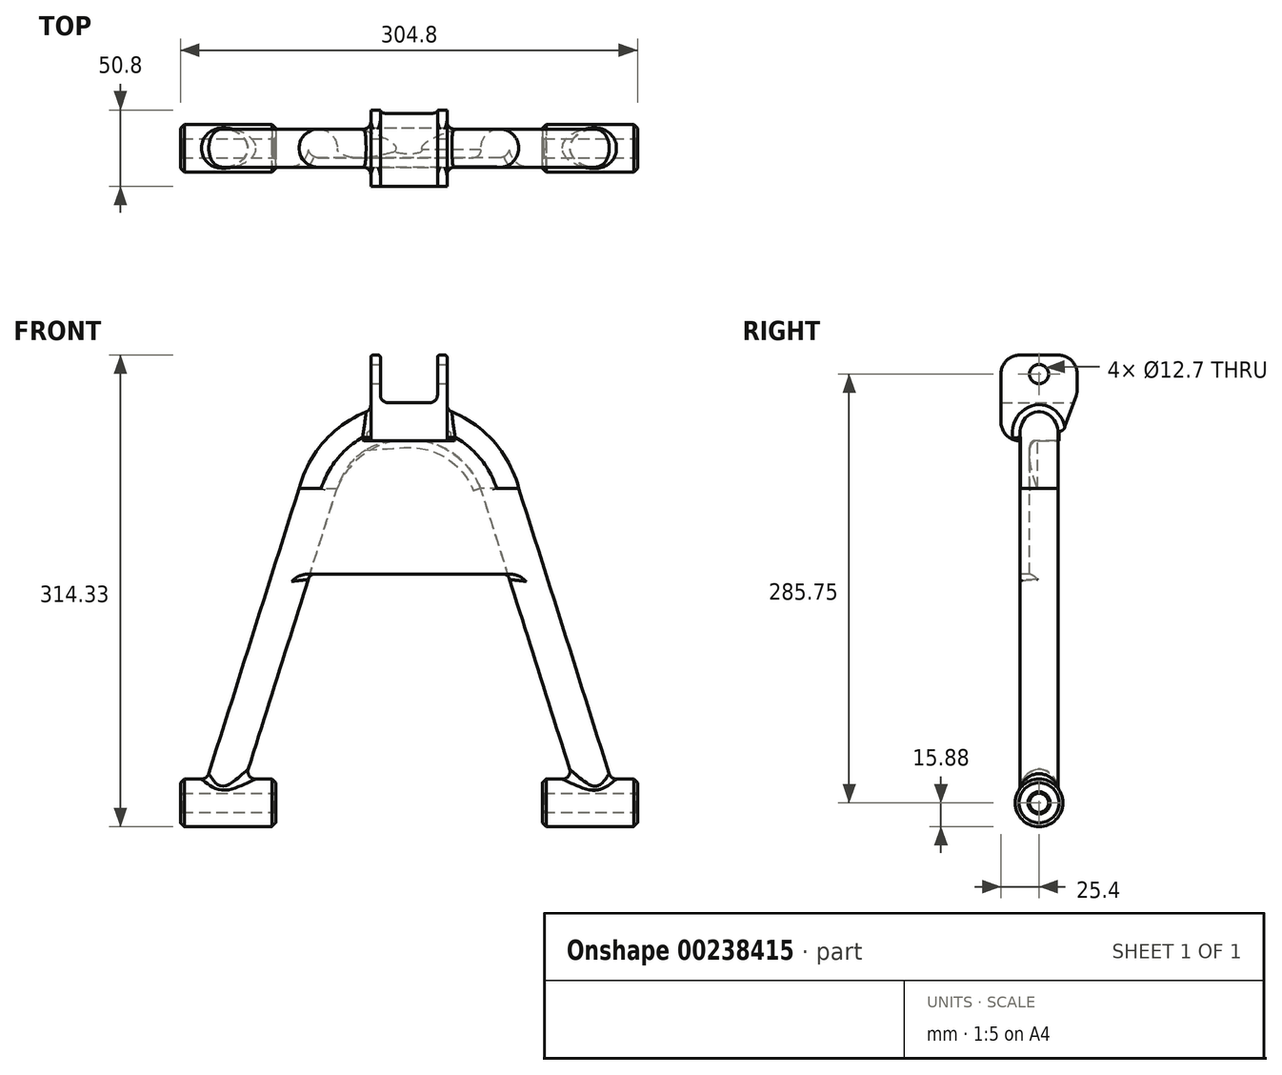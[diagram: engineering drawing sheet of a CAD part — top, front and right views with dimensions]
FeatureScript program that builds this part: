
annotation { "Feature Type Name" : "Feature", "Feature Type Description" : "" }
export const myFeature = defineFeature(function(context is Context, id is Id, definition is map)
    precondition{}
    {
        {
            var Q0;
            Q0=qCreatedBy(makeId("Top.planeOp"),FACE);
            var sketch = newSketch(context, id + "F0", { "sketchPlane" : qUnion([Q0])});
            skLineSegment(sketch, "E0", {"start": v(-127, 0) * mm, "end": v(0, 0) * mm, "construction": true});
            skLineSegment(sketch, "E1", {"start": v(0, 0) * mm, "end": v(127, 0) * mm, "construction": true});
            skCircle(sketch, "E2", {"center": v(-127, 0) * mm, "radius": 12.7 * mm, "construction": true});
            skCircle(sketch, "E3", {"center": v(127, 0) * mm, "radius": 12.7 * mm, "construction": true});
            skSolve(sketch);
        }
        {
            var Q0;
            Q0=qCreatedBy(makeId("Front.planeOp"),FACE);
            var sketch = newSketch(context, id + "F1", { "sketchPlane" : qUnion([Q0])});
            skLineSegment(sketch, "E4", {"start": v(0, 0) * mm, "end": v(0, 254) * mm, "construction": true});
            skArc(sketch, "E5", {"start": v(60.53, 209.69) * mm, "mid": v(0, 254) * mm, "end": v(-60.53, 209.69) * mm, "construction": true});
            skLineSegment(sketch, "E6", {"start": v(0, 0) * mm, "end": v(-127, 0) * mm, "construction": true});
            skLineSegment(sketch, "E7", {"start": v(0, 0) * mm, "end": v(127, 0) * mm, "construction": true});
            skLineSegment(sketch, "E8", {"start": v(-127, 0) * mm, "end": v(-60.53, 209.69) * mm, "construction": true});
            skLineSegment(sketch, "E9", {"start": v(127, 0) * mm, "end": v(60.53, 209.69) * mm, "construction": true});
            skLineSegment(sketch, "E10", {"start": v(-19.05, 271.78) * mm, "end": v(-19.05, 296.93) * mm, "construction": true});
            skLineSegment(sketch, "E11", {"start": v(-20.57, 298.45) * mm, "end": v(-23.88, 298.45) * mm, "construction": true});
            skLineSegment(sketch, "E12", {"start": v(-25.4, 296.93) * mm, "end": v(-25.4, 241.3) * mm, "construction": true});
            skLineSegment(sketch, "E13", {"start": v(-25.4, 241.3) * mm, "end": v(25.4, 241.3) * mm, "construction": true});
            skLineSegment(sketch, "E14", {"start": v(25.4, 241.3) * mm, "end": v(25.4, 296.93) * mm, "construction": true});
            skLineSegment(sketch, "E15", {"start": v(23.88, 298.45) * mm, "end": v(20.57, 298.45) * mm, "construction": true});
            skLineSegment(sketch, "E16", {"start": v(19.05, 296.93) * mm, "end": v(19.05, 271.78) * mm, "construction": true});
            skLineSegment(sketch, "E17", {"start": v(13.97, 266.7) * mm, "end": v(-13.97, 266.7) * mm, "construction": true});
            skPoint(sketch, "E18.orphan", {"position": v(19.05, 254) * mm});
            skPoint(sketch, "E19.visualSharp", {"position": v(-25.4, 298.45) * mm});
            skPoint(sketch, "E20.visualSharp", {"position": v(-19.05, 298.45) * mm});
            skArc(sketch, "E20.filletArc", {"start": v(-19.05, 296.93) * mm, "mid": v(-19.5, 298) * mm, "end": v(-20.57, 298.45) * mm, "construction": true});
            skArc(sketch, "E21.filletArc", {"start": v(-23.88, 298.45) * mm, "mid": v(-24.95, 298) * mm, "end": v(-25.4, 296.93) * mm, "construction": true});
            skPoint(sketch, "E22.visualSharp", {"position": v(19.05, 298.45) * mm});
            skArc(sketch, "E22.filletArc", {"start": v(20.57, 298.45) * mm, "mid": v(19.5, 298) * mm, "end": v(19.05, 296.93) * mm, "construction": true});
            skPoint(sketch, "E23.visualSharp", {"position": v(25.4, 298.45) * mm});
            skArc(sketch, "E23.filletArc", {"start": v(25.4, 296.93) * mm, "mid": v(24.95, 298) * mm, "end": v(23.88, 298.45) * mm, "construction": true});
            skPoint(sketch, "E24.visualSharp", {"position": v(19.05, 266.7) * mm});
            skArc(sketch, "E24.filletArc", {"start": v(13.97, 266.7) * mm, "mid": v(17.56, 268.19) * mm, "end": v(19.05, 271.78) * mm, "construction": true});
            skPoint(sketch, "E25.visualSharp", {"position": v(-19.05, 266.7) * mm});
            skArc(sketch, "E25.filletArc", {"start": v(-19.05, 271.78) * mm, "mid": v(-17.56, 268.19) * mm, "end": v(-13.97, 266.7) * mm, "construction": true});
            skLineSegment(sketch, "E26", {"start": v(0, 0) * mm, "end": v(0, -25.4) * mm, "construction": true});
            skLineSegment(sketch, "E27", {"start": v(0, -25.4) * mm, "end": v(-88.9, -25.4) * mm, "construction": true});
            skLineSegment(sketch, "E28", {"start": v(-88.9, -25.4) * mm, "end": v(-88.9, 25.4) * mm, "construction": true});
            skLineSegment(sketch, "E29", {"start": v(-88.9, 25.4) * mm, "end": v(88.9, 25.4) * mm, "construction": true});
            skLineSegment(sketch, "E30", {"start": v(88.9, 25.4) * mm, "end": v(88.9, -25.4) * mm, "construction": true});
            skLineSegment(sketch, "E31", {"start": v(88.9, -25.4) * mm, "end": v(0, -25.4) * mm, "construction": true});
            skSolve(sketch);
        }
        {
            var Q0;
            Q0=qCreatedBy(makeId("Front.planeOp"),FACE);
            var sketch = newSketch(context, id + "F2", { "sketchPlane" : qUnion([Q0])});
            skLineSegment(sketch, "E32.0", {"start": v(-127, 0) * mm, "end": v(-60.53, 209.69) * mm});
            skArc(sketch, "E33", {"start": v(0, 254) * mm, "mid": v(-37.5, 241.74) * mm, "end": v(-60.53, 209.69) * mm});
            skPoint(sketch, "E32.1.start.orphan", {"position": v(60.53, 209.69) * mm});
            skSolve(sketch);
        }
        {
            var Q0;
            Q0=qCreatedBy(makeId("Top.planeOp"),FACE);
            var sketch = newSketch(context, id + "F3", { "sketchPlane" : qUnion([Q0])});
            skCircle(sketch, "E34.0", {"center": v(-127, 0) * mm, "radius": 12.7 * mm});
            skSolve(sketch);
        }
        {
            var Q0;
            Q0=qCreatedBy(makeId("Right.planeOp"),FACE);
            var sketch = newSketch(context, id + "F4", { "sketchPlane" : qUnion([Q0])});
            skLineSegment(sketch, "E35", {"start": v(0, 0) * mm, "end": v(0, 298.45) * mm, "construction": true});
            skLineSegment(sketch, "E36", {"start": v(0, 298.45) * mm, "end": v(12.7, 298.45) * mm, "construction": true});
            skLineSegment(sketch, "E37", {"start": v(25.4, 285.75) * mm, "end": v(25.4, 275.36) * mm, "construction": true});
            skLineSegment(sketch, "E38", {"start": v(13.46, 247.65) * mm, "end": v(0, 247.65) * mm, "construction": true});
            skLineSegment(sketch, "E39", {"start": v(0, 247.65) * mm, "end": v(-25.4, 247.65) * mm, "construction": true});
            skLineSegment(sketch, "E40", {"start": v(-25.4, 247.65) * mm, "end": v(-25.4, 285.75) * mm, "construction": true});
            skLineSegment(sketch, "E41", {"start": v(-12.7, 298.45) * mm, "end": v(0, 298.45) * mm, "construction": true});
            skLineSegment(sketch, "E42", {"start": v(0, 247.65) * mm, "end": v(0, 298.45) * mm, "construction": true});
            skLineSegment(sketch, "E43", {"start": v(25.4, 273.05) * mm, "end": v(-25.4, 273.05) * mm, "construction": true});
            skCircle(sketch, "E44", {"center": v(0, 285.75) * mm, "radius": 6.35 * mm, "construction": true});
            skLineSegment(sketch, "E45", {"start": v(24.63, 271.02) * mm, "end": v(17.04, 250.16) * mm, "construction": true});
            skPoint(sketch, "E46.newPointA", {"position": v(25.4, 247.65) * mm});
            skArc(sketch, "E46.filletArc", {"start": v(13.46, 247.65) * mm, "mid": v(15.65, 248.34) * mm, "end": v(17.04, 250.16) * mm, "construction": true});
            skArc(sketch, "E47.filletArc", {"start": v(24.63, 271.02) * mm, "mid": v(25.2, 273.15) * mm, "end": v(25.4, 275.36) * mm, "construction": true});
            skPoint(sketch, "E48.visualSharp", {"position": v(25.4, 298.45) * mm});
            skArc(sketch, "E48.filletArc", {"start": v(25.4, 285.75) * mm, "mid": v(21.68, 294.73) * mm, "end": v(12.7, 298.45) * mm, "construction": true});
            skPoint(sketch, "E49.visualSharp", {"position": v(-25.4, 298.45) * mm});
            skArc(sketch, "E49.filletArc", {"start": v(-12.7, 298.45) * mm, "mid": v(-21.68, 294.73) * mm, "end": v(-25.4, 285.75) * mm, "construction": true});
            skLineSegment(sketch, "E50", {"start": v(-25.4, 285.75) * mm, "end": v(-25.4, 298.45) * mm, "construction": true});
            skLineSegment(sketch, "E51", {"start": v(-25.4, 298.45) * mm, "end": v(-12.7, 298.45) * mm, "construction": true});
            skLineSegment(sketch, "E52", {"start": v(12.7, 298.45) * mm, "end": v(25.4, 298.45) * mm, "construction": true});
            skLineSegment(sketch, "E53", {"start": v(13.46, 247.65) * mm, "end": v(25.4, 247.65) * mm, "construction": true});
            skLineSegment(sketch, "E54", {"start": v(25.4, 247.65) * mm, "end": v(25.4, 275.36) * mm, "construction": true});
            skLineSegment(sketch, "E55", {"start": v(25.4, 298.45) * mm, "end": v(25.4, 285.75) * mm, "construction": true});
            skLineSegment(sketch, "E56", {"start": v(13.46, 247.65) * mm, "end": v(13.46, 234.95) * mm, "construction": true});
            skLineSegment(sketch, "E57", {"start": v(13.46, 234.95) * mm, "end": v(25.4, 234.95) * mm, "construction": true});
            skLineSegment(sketch, "E58", {"start": v(25.4, 234.95) * mm, "end": v(25.4, 247.65) * mm, "construction": true});
            skCircle(sketch, "E59", {"center": v(0, 0) * mm, "radius": 15.88 * mm, "construction": true});
            skCircle(sketch, "E60", {"center": v(0, 0) * mm, "radius": 6.35 * mm, "construction": true});
            skSolve(sketch);
        }
        {
            var Q0;
            Q0=qCreatedBy(makeId("Right.planeOp"),FACE);
            var sketch = newSketch(context, id + "F5", { "sketchPlane" : qUnion([Q0])});
            skLineSegment(sketch, "E61.0", {"start": v(24.63, 271.02) * mm, "end": v(17.04, 250.16) * mm});
            skArc(sketch, "E61.1", {"start": v(13.46, 247.65) * mm, "mid": v(15.65, 248.34) * mm, "end": v(17.04, 250.16) * mm});
            skLineSegment(sketch, "E61.3", {"start": v(25.4, 247.65) * mm, "end": v(25.4, 275.36) * mm});
            skArc(sketch, "E61.4", {"start": v(24.63, 271.02) * mm, "mid": v(25.2, 273.15) * mm, "end": v(25.4, 275.36) * mm});
            skArc(sketch, "E61.5", {"start": v(25.4, 285.75) * mm, "mid": v(21.68, 294.73) * mm, "end": v(12.7, 298.45) * mm});
            skLineSegment(sketch, "E61.6", {"start": v(12.7, 298.45) * mm, "end": v(25.4, 298.45) * mm});
            skLineSegment(sketch, "E61.7", {"start": v(25.4, 298.45) * mm, "end": v(25.4, 285.75) * mm});
            skArc(sketch, "E61.8", {"start": v(-12.7, 298.45) * mm, "mid": v(-21.68, 294.73) * mm, "end": v(-25.4, 285.75) * mm});
            skLineSegment(sketch, "E61.9", {"start": v(-25.4, 298.45) * mm, "end": v(-12.7, 298.45) * mm});
            skLineSegment(sketch, "E61.10", {"start": v(-25.4, 285.75) * mm, "end": v(-25.4, 298.45) * mm});
            skLineSegment(sketch, "E62.0", {"start": v(13.46, 247.65) * mm, "end": v(13.46, 234.95) * mm});
            skLineSegment(sketch, "E62.1", {"start": v(13.46, 234.95) * mm, "end": v(25.4, 234.95) * mm});
            skLineSegment(sketch, "E62.2", {"start": v(25.4, 234.95) * mm, "end": v(25.4, 247.65) * mm});
            skPoint(sketch, "E61.2.end.orphan", {"position": v(25.4, 247.65) * mm});
            skPoint(sketch, "E61.2.start.orphan", {"position": v(13.46, 247.65) * mm});
            skSolve(sketch);
        }
        {
            var Q0;
            Q0=qCreatedBy(makeId("Right.planeOp"),FACE);
            var sketch = newSketch(context, id + "F6", { "sketchPlane" : qUnion([Q0])});
            skCircle(sketch, "E63.0", {"center": v(0, 0) * mm, "radius": 15.88 * mm});
            skCircle(sketch, "E63.1", {"center": v(0, 0) * mm, "radius": 6.35 * mm});
            skSolve(sketch);
        }
        {
            var Q0;
            Q0 = qSketchRegion(id + "F3", true);
            var Q1;
            Q1 = qConstructionFilter(qBodyType(qCreatedBy(id + "F2" ,EDGE), BodyType.WIRE), ConstructionObject.NO);
            sweep(context, id + "F7", {"profiles" : qUnion([Q0]), "path" : qUnion([Q1])});
        }
        {
            var Q0;
            Q0=qCreatedBy(makeId("Front.planeOp"),FACE);
            var sketch = newSketch(context, id + "F8", { "sketchPlane" : qUnion([Q0])});
            skPoint(sketch, "E64.0.start.orphan", {"position": v(0, 0) * mm});
            skArc(sketch, "E65.0", {"start": v(60.53, 209.69) * mm, "mid": v(37.5, 241.74) * mm, "end": v(0, 254) * mm});
            skLineSegment(sketch, "E65.1", {"start": v(127, 0) * mm, "end": v(60.53, 209.69) * mm});
            skPoint(sketch, "E66.orphan", {"position": v(-60.53, 209.69) * mm});
            skSolve(sketch);
        }
        {
            var Q0;
            Q0=qCreatedBy(makeId("Top.planeOp"),FACE);
            var sketch = newSketch(context, id + "F9", { "sketchPlane" : qUnion([Q0])});
            skCircle(sketch, "E67.0", {"center": v(127, 0) * mm, "radius": 12.7 * mm});
            skLineSegment(sketch, "E68.0", {"start": v(60.53, 0) * mm, "end": v(-60.53, 0) * mm, "construction": true});
            skLineSegment(sketch, "E68.1", {"start": v(127, 0) * mm, "end": v(60.53, 0) * mm, "construction": true});
            skLineSegment(sketch, "E69.0", {"start": v(60.53, 0) * mm, "end": v(-60.53, 0) * mm});
            skLineSegment(sketch, "E70.0", {"start": v(127, 0) * mm, "end": v(60.53, 0) * mm});
            skSolve(sketch);
        }
        {
            var Q0;
            Q0 = qSketchRegion(id + "F9", true);
            var Q1;
            Q1 = qConstructionFilter(qBodyType(qCreatedBy(id + "F8" ,EDGE), BodyType.WIRE), ConstructionObject.NO);
            sweep(context, id + "F10", {"profiles" : qUnion([Q0]), "path" : qUnion([Q1])});
        }
        {
            var Q0;
            Q0=qCreatedBy(makeId("Front.planeOp"),FACE);
            var sketch = newSketch(context, id + "F11", { "sketchPlane" : qUnion([Q0])});
            skArc(sketch, "E71.0", {"start": v(60.53, 209.69) * mm, "mid": v(0, 254) * mm, "end": v(-60.53, 209.69) * mm, "construction": true});
            skLineSegment(sketch, "E71.1", {"start": v(-127, 0) * mm, "end": v(-60.53, 209.69) * mm, "construction": true});
            skLineSegment(sketch, "E71.2", {"start": v(127, 0) * mm, "end": v(60.53, 209.69) * mm, "construction": true});
            skLineSegment(sketch, "E72", {"start": v(78.7, 152.4) * mm, "end": v(-78.7, 152.4) * mm, "construction": true});
            skSolve(sketch);
        }
        {
            var Q0;
            Q0=qCreatedBy(makeId("Front.planeOp"),FACE);
            var sketch = newSketch(context, id + "F12", { "sketchPlane" : qUnion([Q0])});
            skArc(sketch, "E73.0", {"start": v(60.53, 209.69) * mm, "mid": v(0, 254) * mm, "end": v(-60.53, 209.69) * mm});
            skLineSegment(sketch, "E73.1", {"start": v(-78.7, 152.4) * mm, "end": v(-60.53, 209.69) * mm});
            skLineSegment(sketch, "E73.2", {"start": v(78.7, 152.4) * mm, "end": v(-78.7, 152.4) * mm});
            skLineSegment(sketch, "E73.3", {"start": v(78.7, 152.4) * mm, "end": v(60.53, 209.69) * mm});
            skPoint(sketch, "E74.orphan", {"position": v(-127, 0) * mm});
            skPoint(sketch, "E75.orphan", {"position": v(127, 0) * mm});
            skSolve(sketch);
        }
        {
            var Q0;
            Q0 = qSketchRegion(id + "F12", true);
            var Q1;
            Q1=makeQuery(id+"F7.opSweep","SWEPT_FACE",FACE,{"disambiguationData":[OSD([sQuery(id+"F2.wireOp",EDGE,"E32.0"),sQuery(id+"F3.wireOp",EDGE,"E34.0")])]});
            extrude(context, id + "F13", {"entities" : qUnion([Q0]), "depth" : 12.7 * mm, "endBoundEntityFace" : qUnion([Q1]), "offsetDistance" : 25.4 * mm, "hasSecondDirection" : true, "secondDirectionOppositeDirection" : true, "secondDirectionDepth" : -6.35 * mm});
        }
        {
            var Q0;
            Q0=qCreatedBy(makeId("Front.planeOp"),FACE);
            var sketch = newSketch(context, id + "F14", { "sketchPlane" : qUnion([Q0])});
            skLineSegment(sketch, "E76.0", {"start": v(-25.4, 296.93) * mm, "end": v(-25.4, 241.3) * mm});
            skArc(sketch, "E76.1", {"start": v(-23.88, 298.45) * mm, "mid": v(-24.95, 298) * mm, "end": v(-25.4, 296.93) * mm});
            skLineSegment(sketch, "E76.2", {"start": v(-20.57, 298.45) * mm, "end": v(-23.88, 298.45) * mm});
            skArc(sketch, "E76.3", {"start": v(-19.05, 296.93) * mm, "mid": v(-19.5, 298) * mm, "end": v(-20.57, 298.45) * mm});
            skLineSegment(sketch, "E76.4", {"start": v(-19.05, 271.78) * mm, "end": v(-19.05, 296.93) * mm});
            skArc(sketch, "E76.5", {"start": v(-19.05, 271.78) * mm, "mid": v(-17.56, 268.19) * mm, "end": v(-13.97, 266.7) * mm});
            skLineSegment(sketch, "E76.6", {"start": v(13.97, 266.7) * mm, "end": v(-13.97, 266.7) * mm});
            skArc(sketch, "E76.7", {"start": v(13.97, 266.7) * mm, "mid": v(17.56, 268.19) * mm, "end": v(19.05, 271.78) * mm});
            skLineSegment(sketch, "E76.8", {"start": v(19.05, 296.93) * mm, "end": v(19.05, 271.78) * mm});
            skArc(sketch, "E76.9", {"start": v(20.57, 298.45) * mm, "mid": v(19.5, 298) * mm, "end": v(19.05, 296.93) * mm});
            skLineSegment(sketch, "E76.10", {"start": v(23.88, 298.45) * mm, "end": v(20.57, 298.45) * mm});
            skArc(sketch, "E76.11", {"start": v(25.4, 296.93) * mm, "mid": v(24.95, 298) * mm, "end": v(23.88, 298.45) * mm});
            skLineSegment(sketch, "E76.12", {"start": v(25.4, 241.3) * mm, "end": v(25.4, 296.93) * mm});
            skLineSegment(sketch, "E76.13", {"start": v(-25.4, 241.3) * mm, "end": v(25.4, 241.3) * mm});
            skSolve(sketch);
        }
        {
            var Q0;
            Q0=makeQuery(id+"F14.imprint","IMPRINT",FACE,{"disambiguationData":[TD([[makeQuery(id+"F14.imprint","IMPRINT",EDGE,{"derivedFrom":sQuery(id+"F14.wireOp",EDGE,"E76.0")}),1.0]])]});
            var Q1;
            Q1 = qConstructionFilter(qBodyType(qCreatedBy(id + "F14" ,EDGE), BodyType.WIRE), ConstructionObject.NO);
            extrude(context, id + "F15", {"entities" : qUnion([Q0]), "surfaceEntities" : qUnion([Q1]), "depth" : 25.4 * mm, "offsetDistance" : 25.4 * mm, "hasSecondDirection" : true, "secondDirectionOppositeDirection" : true, "secondDirectionDepth" : 25.4 * mm});
        }
        {
            var Q0;
            Q0=makeQuery(id+"F13.opExtrude","CAP_EDGE",EDGE,{"disambiguationData":[OSD([sQuery(id+"F12.wireOp",EDGE,"E73.1")])],"isStart":false});
            fillet(context, id + "F16", {"entities" : qUnion([Q0]), "radius" : 5.08 * mm, "tangentPropagation" : true, "allowEdgeOverflow" : false});
        }
        {
            var Q0;
            Q0=qCreatedBy(makeId("Right.planeOp"),FACE);
            var sketch = newSketch(context, id + "F17", { "sketchPlane" : qUnion([Q0])});
            skCircle(sketch, "E77.0", {"center": v(0, 285.75) * mm, "radius": 6.35 * mm});
            skSolve(sketch);
        }
        {
            var Q0;
            Q0 = qSketchRegion(id + "F17", true);
            var Q1;
            Q1 = qConstructionFilter(qBodyType(qCreatedBy(id + "F17" ,EDGE), BodyType.WIRE), ConstructionObject.NO);
            extrude(context, id + "F18", {"entities" : qUnion([Q0]), "operationType" : NewBodyOperationType.REMOVE, "surfaceEntities" : qUnion([Q1]), "endBound" : BoundingType.THROUGH_ALL, "oppositeDirection" : true, "depth" : 25.4 * mm, "offsetDistance" : 25.4 * mm, "hasSecondDirection" : true, "secondDirectionOppositeDirection" : false, "secondDirectionDepth" : 25.4 * mm});
        }
        {
            var Q0;
            Q0 = qSketchRegion(id + "F5", true);
            extrude(context, id + "F19", {"entities" : qUnion([Q0]), "operationType" : NewBodyOperationType.REMOVE, "endBound" : BoundingType.THROUGH_ALL, "oppositeDirection" : true, "depth" : 25.4 * mm, "offsetDistance" : 25.4 * mm, "hasSecondDirection" : true, "secondDirectionBound" : SecondDirectionBoundingType.THROUGH_ALL, "secondDirectionOppositeDirection" : false, "secondDirectionDepth" : 25.4 * mm});
        }
        {
            var Q0;
            Q0=makeQuery(id+"F19.boolean.opBoolean","COPY",EDGE,{"derivedFrom":makeQuery(id+"F19.opExtrude","SWEPT_EDGE",EDGE,{"disambiguationData":[OSD([sQuery(id+"F5.wireOp",EDGE,"E61.1"),sQuery(id+"F5.wireOp",EDGE,"E62.0")])]})});
            fillet(context, id + "F20", {"entities" : qUnion([Q0]), "radius" : 1.52 * mm, "tangentPropagation" : true, "allowEdgeOverflow" : false});
        }
        {
            var Q0;
            Q0=makeQuery(id+"F15.opExtrude","CAP_EDGE",EDGE,{"disambiguationData":[OSD([sQuery(id+"F14.wireOp",EDGE,"E76.13")])],"isStart":false});
            fillet(context, id + "F21", {"entities" : qUnion([Q0]), "radius" : 12.7 * mm, "tangentPropagation" : true, "allowEdgeOverflow" : false});
        }
        {
            var Q0;
            Q0 = qSketchRegion(id + "F6", true);
            var Q1;
            Q1 = qConstructionFilter(qBodyType(qCreatedBy(id + "F6" ,EDGE), BodyType.WIRE), ConstructionObject.NO);
            extrude(context, id + "F22", {"entities" : qUnion([Q0]), "surfaceEntities" : qUnion([Q1]), "depth" : 152.4 * mm, "offsetDistance" : 25.4 * mm, "hasSecondDirection" : true, "secondDirectionOppositeDirection" : true, "secondDirectionDepth" : 152.4 * mm});
        }
        {
            var Q0;
            Q0=qCreatedBy(makeId("Right.planeOp"),FACE);
            var sketch = newSketch(context, id + "F23", { "sketchPlane" : qUnion([Q0])});
            skCircle(sketch, "E78.0", {"center": v(0, 0) * mm, "radius": 6.35 * mm});
            skSolve(sketch);
        }
        {
            var Q0;
            Q0 = qSketchRegion(id + "F23", true);
            extrude(context, id + "F24", {"entities" : qUnion([Q0]), "operationType" : NewBodyOperationType.REMOVE, "endBound" : BoundingType.THROUGH_ALL, "oppositeDirection" : true, "depth" : 25.4 * mm, "offsetDistance" : 25.4 * mm, "hasSecondDirection" : true, "secondDirectionBound" : SecondDirectionBoundingType.THROUGH_ALL, "secondDirectionOppositeDirection" : false, "secondDirectionDepth" : 25.4 * mm});
        }
        {
            var Q0;
            Q0=qCreatedBy(makeId("Front.planeOp"),FACE);
            var sketch = newSketch(context, id + "F25", { "sketchPlane" : qUnion([Q0])});
            skLineSegment(sketch, "E79.0", {"start": v(-88.9, 25.4) * mm, "end": v(88.9, 25.4) * mm});
            skLineSegment(sketch, "E79.1", {"start": v(-88.9, -25.4) * mm, "end": v(-88.9, 25.4) * mm});
            skLineSegment(sketch, "E79.2", {"start": v(0, -25.4) * mm, "end": v(-88.9, -25.4) * mm});
            skLineSegment(sketch, "E79.3", {"start": v(88.9, -25.4) * mm, "end": v(0, -25.4) * mm});
            skLineSegment(sketch, "E79.4", {"start": v(88.9, 25.4) * mm, "end": v(88.9, -25.4) * mm});
            skSolve(sketch);
        }
        {
            var Q0;
            Q0 = qSketchRegion(id + "F25", true);
            var Q1;
            Q1 = qConstructionFilter(qBodyType(qCreatedBy(id + "F25" ,EDGE), BodyType.WIRE), ConstructionObject.NO);
            extrude(context, id + "F26", {"entities" : qUnion([Q0]), "operationType" : NewBodyOperationType.REMOVE, "surfaceEntities" : qUnion([Q1]), "endBound" : BoundingType.THROUGH_ALL, "oppositeDirection" : true, "depth" : 25.4 * mm, "offsetDistance" : 25.4 * mm, "hasSecondDirection" : true, "secondDirectionBound" : SecondDirectionBoundingType.THROUGH_ALL, "secondDirectionOppositeDirection" : false, "secondDirectionDepth" : 25.4 * mm});
        }
        {
            var Q0;
            Q0=makeQuery(id+"F26.boolean.opBoolean","INTERSECT",EDGE,{"derivedFrom":[makeQuery(id+"F22.opExtrude","SWEPT_FACE",FACE,{"disambiguationData":[OSD([sQuery(id+"F6.wireOp",EDGE,"E63.0")])]}),makeQuery(id+"F26.opExtrude","SWEPT_FACE",FACE,{"disambiguationData":[OSD([sQuery(id+"F25.wireOp",EDGE,"E79.1")])]})]});
            var Q1;
            Q1=makeQuery(id+"F22.opExtrude","CAP_EDGE",EDGE,{"disambiguationData":[OSD([sQuery(id+"F6.wireOp",EDGE,"E63.0")])],"isStart":true});
            var Q2;
            Q2=makeQuery(id+"F22.opExtrude","CAP_EDGE",EDGE,{"disambiguationData":[OSD([sQuery(id+"F6.wireOp",EDGE,"E63.0")])],"isStart":false});
            var Q3;
            Q3=makeQuery(id+"F26.boolean.opBoolean","INTERSECT",EDGE,{"derivedFrom":[makeQuery(id+"F22.opExtrude","SWEPT_FACE",FACE,{"disambiguationData":[OSD([sQuery(id+"F6.wireOp",EDGE,"E63.0")])]}),makeQuery(id+"F26.opExtrude","SWEPT_FACE",FACE,{"disambiguationData":[OSD([sQuery(id+"F25.wireOp",EDGE,"E79.4")])]})]});
            chamfer(context, id + "F27", {"entities" : qUnion([Q0, Q1, Q2, Q3]), "width" : 2.54 * mm, "tangentPropagation" : true});
        }
        {
            var Q0;
            Q0=makeQuery(id+"F26.boolean.opBoolean","INTERSECT",EDGE,{"derivedFrom":[makeQuery(id+"F22.opExtrude","SWEPT_FACE",FACE,{"disambiguationData":[OSD([sQuery(id+"F6.wireOp",EDGE,"E63.1")])]}),makeQuery(id+"F26.opExtrude","SWEPT_FACE",FACE,{"disambiguationData":[OSD([sQuery(id+"F25.wireOp",EDGE,"E79.1")])]})]});
            var Q1;
            Q1=makeQuery(id+"F22.opExtrude","CAP_EDGE",EDGE,{"disambiguationData":[OSD([sQuery(id+"F6.wireOp",EDGE,"E63.1")])],"isStart":false});
            var Q2;
            Q2=makeQuery(id+"F26.boolean.opBoolean","INTERSECT",EDGE,{"derivedFrom":[makeQuery(id+"F22.opExtrude","SWEPT_FACE",FACE,{"disambiguationData":[OSD([sQuery(id+"F6.wireOp",EDGE,"E63.1")])]}),makeQuery(id+"F26.opExtrude","SWEPT_FACE",FACE,{"disambiguationData":[OSD([sQuery(id+"F25.wireOp",EDGE,"E79.4")])]})]});
            var Q3;
            Q3=makeQuery(id+"F22.opExtrude","CAP_EDGE",EDGE,{"disambiguationData":[OSD([sQuery(id+"F6.wireOp",EDGE,"E63.1")])],"isStart":true});
            chamfer(context, id + "F28", {"entities" : qUnion([Q0, Q1, Q2, Q3]), "width" : 1.02 * mm, "tangentPropagation" : true});
        }
        {
            var Q0;
            Q0=makeQuery(id+"F13.opExtrude","SWEPT_BODY",BODY,{"disambiguationData":[OSD([sQuery(id+"F12.wireOp",EDGE,"E73.0"),sQuery(id+"F12.wireOp",EDGE,"E73.1"),sQuery(id+"F12.wireOp",EDGE,"E73.2"),sQuery(id+"F12.wireOp",EDGE,"E73.3")])]});
            var Q1;
            Q1=makeQuery(id+"F10.opSweep","SWEPT_BODY",BODY,{"disambiguationData":[OSD([sQuery(id+"F8.wireOp",EDGE,"E65.1"),sQuery(id+"F9.wireOp",EDGE,"E67.0")])]});
            var Q2;
            Q2=makeQuery(id+"F7.opSweep","SWEPT_BODY",BODY,{"disambiguationData":[OSD([sQuery(id+"F2.wireOp",EDGE,"E33"),sQuery(id+"F3.wireOp",EDGE,"E34.0")])]});
            var Q3;
            Q3=makeQuery(id+"F15.opExtrude","SWEPT_BODY",BODY,{"disambiguationData":[OSD([sQuery(id+"F14.wireOp",EDGE,"E76.0"),sQuery(id+"F14.wireOp",EDGE,"E76.1"),sQuery(id+"F14.wireOp",EDGE,"E76.2"),sQuery(id+"F14.wireOp",EDGE,"E76.3"),sQuery(id+"F14.wireOp",EDGE,"E76.4"),sQuery(id+"F14.wireOp",EDGE,"E76.5"),sQuery(id+"F14.wireOp",EDGE,"E76.6"),sQuery(id+"F14.wireOp",EDGE,"E76.7"),sQuery(id+"F14.wireOp",EDGE,"E76.8"),sQuery(id+"F14.wireOp",EDGE,"E76.9"),sQuery(id+"F14.wireOp",EDGE,"E76.10"),sQuery(id+"F14.wireOp",EDGE,"E76.11"),sQuery(id+"F14.wireOp",EDGE,"E76.12"),sQuery(id+"F14.wireOp",EDGE,"E76.13")])]});
            var Q4;
            Q4=makeQuery(id+"F26.boolean.opBoolean","SPLIT",BODY,{"disambiguationData":[OD(1.0)],"derivedFrom":makeQuery(id+"F22.opExtrude","SWEPT_BODY",BODY,{"disambiguationData":[OSD([sQuery(id+"F6.wireOp",EDGE,"E63.0"),sQuery(id+"F6.wireOp",EDGE,"E63.1")])]})});
            var Q5;
            Q5=makeQuery(id+"F26.boolean.opBoolean","SPLIT",BODY,{"disambiguationData":[OD(0.0)],"derivedFrom":makeQuery(id+"F22.opExtrude","SWEPT_BODY",BODY,{"disambiguationData":[OSD([sQuery(id+"F6.wireOp",EDGE,"E63.0"),sQuery(id+"F6.wireOp",EDGE,"E63.1")])]})});
            booleanBodies(context, id + "F29", {"operationType" : BooleanOperationType.UNION, "tools" : qUnion([Q0, Q1, Q2, Q3, Q4, Q5])});
        }
        {
            var Q0;
            Q0=makeQuery(id+"F29.opBoolean","INTERSECT",EDGE,{"derivedFrom":[makeQuery(id+"F13.opExtrude","CAP_FACE",FACE,{"disambiguationData":[OSD([sQuery(id+"F12.wireOp",EDGE,"E73.0"),sQuery(id+"F12.wireOp",EDGE,"E73.1"),sQuery(id+"F12.wireOp",EDGE,"E73.2"),sQuery(id+"F12.wireOp",EDGE,"E73.3")])],"isStart":true}),makeQuery(id+"F10.opSweep","SWEPT_FACE",FACE,{"disambiguationData":[OSD([sQuery(id+"F8.wireOp",EDGE,"E65.1"),sQuery(id+"F9.wireOp",EDGE,"E67.0")])]})]});
            var Q1;
            Q1=makeQuery(id+"F29.opBoolean","INTERSECT",EDGE,{"derivedFrom":[makeQuery(id+"F10.opSweep","SWEPT_FACE",FACE,{"disambiguationData":[OSD([sQuery(id+"F8.wireOp",EDGE,"E65.0"),sQuery(id+"F9.wireOp",EDGE,"E67.0")])]}),makeQuery(id+"F13.opExtrude","CAP_FACE",FACE,{"disambiguationData":[OSD([sQuery(id+"F12.wireOp",EDGE,"E73.0"),sQuery(id+"F12.wireOp",EDGE,"E73.1"),sQuery(id+"F12.wireOp",EDGE,"E73.2"),sQuery(id+"F12.wireOp",EDGE,"E73.3")])],"isStart":true})]});
            var Q2;
            Q2=makeQuery(id+"F29.opBoolean","INTERSECT",EDGE,{"derivedFrom":[makeQuery(id+"F13.opExtrude","CAP_FACE",FACE,{"disambiguationData":[OSD([sQuery(id+"F12.wireOp",EDGE,"E73.0"),sQuery(id+"F12.wireOp",EDGE,"E73.1"),sQuery(id+"F12.wireOp",EDGE,"E73.2"),sQuery(id+"F12.wireOp",EDGE,"E73.3")])],"isStart":true}),makeQuery(id+"F7.opSweep","SWEPT_FACE",FACE,{"disambiguationData":[OSD([sQuery(id+"F2.wireOp",EDGE,"E32.0"),sQuery(id+"F3.wireOp",EDGE,"E34.0")])]})]});
            var Q3;
            Q3=makeQuery(id+"F29.opBoolean","INTERSECT",EDGE,{"derivedFrom":[makeQuery(id+"F16.opFillet","BLEND_FACE",FACE,{"disambiguationData":[OSD([sQuery(id+"F12.wireOp",EDGE,"E73.3")])]}),makeQuery(id+"F10.opSweep","SWEPT_FACE",FACE,{"disambiguationData":[OSD([sQuery(id+"F8.wireOp",EDGE,"E65.1"),sQuery(id+"F9.wireOp",EDGE,"E67.0")])]})]});
            var Q4;
            Q4=makeQuery(id+"F29.opBoolean","INTERSECT",EDGE,{"derivedFrom":[makeQuery(id+"F10.opSweep","SWEPT_FACE",FACE,{"disambiguationData":[OSD([sQuery(id+"F8.wireOp",EDGE,"E65.0"),sQuery(id+"F9.wireOp",EDGE,"E67.0")])]}),makeQuery(id+"F16.opFillet","BLEND_FACE",FACE,{"disambiguationData":[OSD([sQuery(id+"F12.wireOp",EDGE,"E73.0")])]})]});
            var Q5;
            Q5=makeQuery(id+"F29.opBoolean","INTERSECT",EDGE,{"derivedFrom":[makeQuery(id+"F16.opFillet","BLEND_FACE",FACE,{"disambiguationData":[OSD([sQuery(id+"F12.wireOp",EDGE,"E73.1")])]}),makeQuery(id+"F7.opSweep","SWEPT_FACE",FACE,{"disambiguationData":[OSD([sQuery(id+"F2.wireOp",EDGE,"E32.0"),sQuery(id+"F3.wireOp",EDGE,"E34.0")])]})]});
            var Q6;
            Q6=makeQuery(id+"F29.opBoolean","INTERSECT",EDGE,{"derivedFrom":[makeQuery(id+"F7.opSweep","SWEPT_FACE",FACE,{"disambiguationData":[OSD([sQuery(id+"F2.wireOp",EDGE,"E33"),sQuery(id+"F3.wireOp",EDGE,"E34.0")])]}),makeQuery(id+"F16.opFillet","BLEND_FACE",FACE,{"disambiguationData":[OSD([sQuery(id+"F12.wireOp",EDGE,"E73.0")])]})]});
            fillet(context, id + "F30", {"entities" : qUnion([Q0, Q1, Q2, Q3, Q4, Q5, Q6]), "radius" : 5.08 * mm, "tangentPropagation" : true, "allowEdgeOverflow" : false});
        }
        {
            var Q0;
            Q0=makeQuery(id+"F29.opBoolean","INTERSECT",EDGE,{"derivedFrom":[makeQuery(id+"F13.opExtrude","SWEPT_FACE",FACE,{"disambiguationData":[OSD([sQuery(id+"F12.wireOp",EDGE,"E73.2")])]}),makeQuery(id+"F7.opSweep","SWEPT_FACE",FACE,{"disambiguationData":[OSD([sQuery(id+"F2.wireOp",EDGE,"E32.0"),sQuery(id+"F3.wireOp",EDGE,"E34.0")])]})]});
            var Q1;
            Q1=makeQuery(id+"F29.opBoolean","INTERSECT",EDGE,{"derivedFrom":[makeQuery(id+"F13.opExtrude","SWEPT_FACE",FACE,{"disambiguationData":[OSD([sQuery(id+"F12.wireOp",EDGE,"E73.2")])]}),makeQuery(id+"F10.opSweep","SWEPT_FACE",FACE,{"disambiguationData":[OSD([sQuery(id+"F8.wireOp",EDGE,"E65.1"),sQuery(id+"F9.wireOp",EDGE,"E67.0")])]})]});
            fillet(context, id + "F31", {"entities" : qUnion([Q0, Q1]), "radius" : 5.08 * mm, "tangentPropagation" : true, "allowEdgeOverflow" : false});
        }
        {
            var Q0;
            Q0=makeQuery(id+"F29.opBoolean","INTERSECT",EDGE,{"derivedFrom":[makeQuery(id+"F10.opSweep","SWEPT_FACE",FACE,{"disambiguationData":[OSD([sQuery(id+"F8.wireOp",EDGE,"E65.0"),sQuery(id+"F9.wireOp",EDGE,"E67.0")])]}),makeQuery(id+"F15.opExtrude","SWEPT_FACE",FACE,{"disambiguationData":[OSD([sQuery(id+"F14.wireOp",EDGE,"E76.12")])]})]});
            var Q1;
            {var subQ0=sQuery(id+"F14.wireOp",EDGE,"E76.13");Q1=makeQuery(id+"F21.opFillet","BLEND_EDGE",EDGE,{"blendedFrom":[makeQuery(id+"F15.opExtrude","CAP_EDGE",EDGE,{"disambiguationData":[OSD([subQ0])],"isStart":false}),makeQuery(id+"F15.opExtrude","SWEPT_FACE",FACE,{"disambiguationData":[OSD([subQ0])]})],"blendedInto":[makeQuery(id+"F15.opExtrude","SWEPT_FACE",FACE,{"disambiguationData":[OSD([subQ0])]})]});}
            var Q2;
            Q2=makeQuery(id+"F29.opBoolean","INTERSECT",EDGE,{"derivedFrom":[makeQuery(id+"F7.opSweep","SWEPT_FACE",FACE,{"disambiguationData":[OSD([sQuery(id+"F2.wireOp",EDGE,"E33"),sQuery(id+"F3.wireOp",EDGE,"E34.0")])]}),makeQuery(id+"F15.opExtrude","SWEPT_FACE",FACE,{"disambiguationData":[OSD([sQuery(id+"F14.wireOp",EDGE,"E76.0")])]})]});
            var Q3;
            {var subQ0=sQuery(id+"F6.wireOp",EDGE,"E63.0");Q3=makeQuery(id+"F29.opBoolean","INTERSECT",EDGE,{"derivedFrom":[makeQuery(id+"F7.opSweep","SWEPT_FACE",FACE,{"disambiguationData":[OSD([sQuery(id+"F2.wireOp",EDGE,"E32.0"),sQuery(id+"F3.wireOp",EDGE,"E34.0")])]}),makeQuery(id+"F26.boolean.opBoolean","SPLIT",FACE,{"disambiguationData":[TD([makeQuery(id+"F26.opExtrude","SWEPT_FACE",FACE,{"disambiguationData":[OSD([sQuery(id+"F25.wireOp",EDGE,"E79.1")])]})])],"derivedFrom":makeQuery(id+"F22.opExtrude","SWEPT_FACE",FACE,{"disambiguationData":[OSD([subQ0])]})})]});}
            var Q4;
            {var subQ0=sQuery(id+"F6.wireOp",EDGE,"E63.0");Q4=makeQuery(id+"F29.opBoolean","INTERSECT",EDGE,{"derivedFrom":[makeQuery(id+"F10.opSweep","SWEPT_FACE",FACE,{"disambiguationData":[OSD([sQuery(id+"F8.wireOp",EDGE,"E65.1"),sQuery(id+"F9.wireOp",EDGE,"E67.0")])]}),makeQuery(id+"F26.boolean.opBoolean","SPLIT",FACE,{"disambiguationData":[TD([makeQuery(id+"F26.opExtrude","SWEPT_FACE",FACE,{"disambiguationData":[OSD([sQuery(id+"F25.wireOp",EDGE,"E79.4")])]})])],"derivedFrom":makeQuery(id+"F22.opExtrude","SWEPT_FACE",FACE,{"disambiguationData":[OSD([subQ0])]})})]});}
            fillet(context, id + "F32", {"entities" : qUnion([Q0, Q1, Q2, Q3, Q4]), "radius" : 5.08 * mm, "tangentPropagation" : true, "allowEdgeOverflow" : false});
        }
    });
